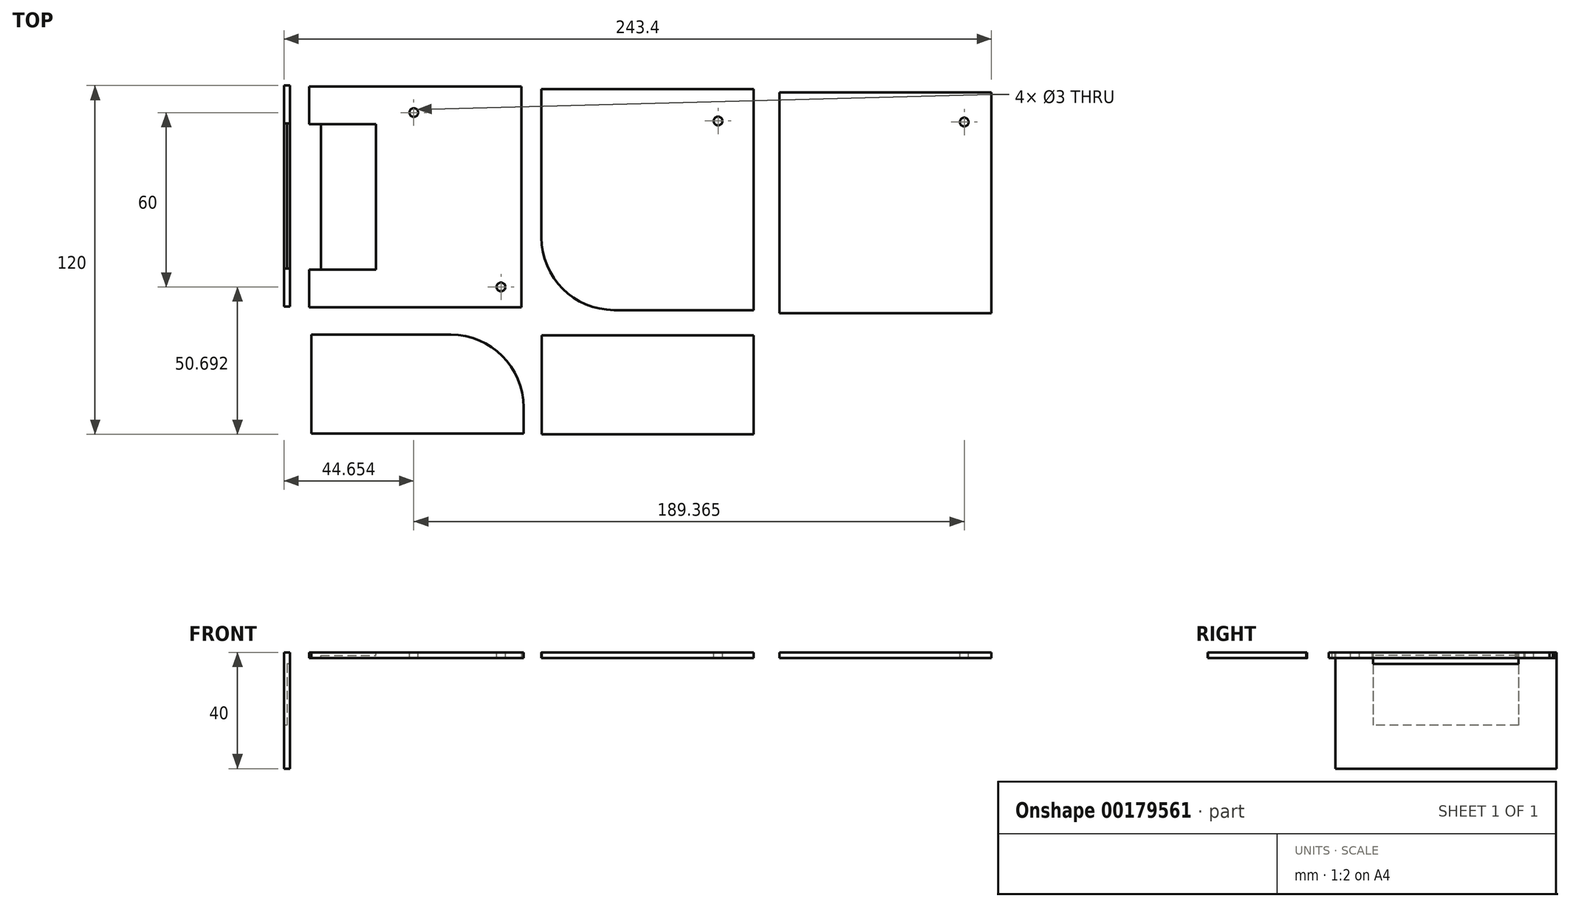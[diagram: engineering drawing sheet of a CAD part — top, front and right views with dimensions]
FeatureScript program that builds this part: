
annotation { "Feature Type Name" : "Feature", "Feature Type Description" : "" }
export const myFeature = defineFeature(function(context is Context, id is Id, definition is map)
    precondition{}
    {
        {
            var Q0;
            Q0=qCreatedBy(makeId("Top.planeOp"),FACE);
            var sketch = newSketch(context, id + "F0", { "sketchPlane" : qUnion([Q0])});
            skLineSegment(sketch, "E0.bottom", {"start": v(-79.9, 85.7) * mm, "end": v(-6.9, 85.7) * mm});
            skLineSegment(sketch, "E0.top", {"start": v(-79.9, 9.7) * mm, "end": v(-6.9, 9.7) * mm});
            skLineSegment(sketch, "E0.left", {"start": v(-79.9, 85.7) * mm, "end": v(-79.9, 9.7) * mm});
            skLineSegment(sketch, "E0.right", {"start": v(-6.9, 85.7) * mm, "end": v(-6.9, 9.7) * mm});
            skSolve(sketch);
        }
        {
            var Q0;
            Q0=qSketchRegion(id+"F0",true);
            extrude(context, id + "F1", {"entities" : qUnion([Q0]), "depth" : 2 * mm});
        }
        {
            var Q0;
            Q0=qCreatedBy(makeId("Top.planeOp"),FACE);
            var sketch = newSketch(context, id + "F2", { "sketchPlane" : qUnion([Q0])});
            skLineSegment(sketch, "E1.bottom", {"start": v(0, 84.75) * mm, "end": v(73, 84.75) * mm});
            skLineSegment(sketch, "E1.top", {"start": v(25, 8.75) * mm, "end": v(73, 8.75) * mm});
            skLineSegment(sketch, "E1.left", {"start": v(0, 84.75) * mm, "end": v(0, 33.75) * mm});
            skLineSegment(sketch, "E1.right", {"start": v(73, 84.75) * mm, "end": v(73, 8.75) * mm});
            skPoint(sketch, "E2.visualSharp", {"position": v(0, 8.75) * mm});
            skArc(sketch, "E2.filletArc", {"start": v(0, 33.75) * mm, "mid": v(7.33, 16.07) * mm, "end": v(25, 8.75) * mm});
            skSolve(sketch);
        }
        {
            var Q0;
            Q0=qSketchRegion(id+"F2",true);
            extrude(context, id + "F3", {"entities" : qUnion([Q0]), "depth" : 2 * mm});
        }
        {
            var Q0;
            Q0=qCreatedBy(makeId("Top.planeOp"),FACE);
            var sketch = newSketch(context, id + "F4", { "sketchPlane" : qUnion([Q0])});
            skLineSegment(sketch, "E3.bottom", {"start": v(-79.15, 0.26) * mm, "end": v(-31.15, 0.26) * mm});
            skLineSegment(sketch, "E3.top", {"start": v(-79.15, -33.74) * mm, "end": v(-6.15, -33.74) * mm});
            skLineSegment(sketch, "E3.left", {"start": v(-79.15, 0.26) * mm, "end": v(-79.15, -33.74) * mm});
            skLineSegment(sketch, "E3.right", {"start": v(-6.15, -24.74) * mm, "end": v(-6.15, -33.74) * mm});
            skPoint(sketch, "E4.visualSharp", {"position": v(-6.15, 0.26) * mm});
            skArc(sketch, "E4.filletArc", {"start": v(-6.15, -24.74) * mm, "mid": v(-13.47, -7.06) * mm, "end": v(-31.15, 0.26) * mm});
            skSolve(sketch);
        }
        {
            var Q0;
            Q0=qSketchRegion(id+"F4",true);
            extrude(context, id + "F5", {"entities" : qUnion([Q0]), "depth" : 2 * mm});
        }
        {
            var Q0;
            Q0=qCreatedBy(makeId("Top.planeOp"),FACE);
            var sketch = newSketch(context, id + "F6", { "sketchPlane" : qUnion([Q0])});
            skLineSegment(sketch, "E5.bottom", {"start": v(0.04, 0) * mm, "end": v(73.04, 0) * mm});
            skLineSegment(sketch, "E5.top", {"start": v(0.04, -34) * mm, "end": v(73.04, -34) * mm});
            skLineSegment(sketch, "E5.left", {"start": v(0.04, 0) * mm, "end": v(0.04, -34) * mm});
            skLineSegment(sketch, "E5.right", {"start": v(73.04, 0) * mm, "end": v(73.04, -34) * mm});
            skSolve(sketch);
        }
        {
            var Q0;
            Q0=qSketchRegion(id+"F6",true);
            extrude(context, id + "F7", {"entities" : qUnion([Q0]), "depth" : 2 * mm});
        }
        {
            var Q0;
            Q0=qCreatedBy(makeId("Top.planeOp"),FACE);
            var sketch = newSketch(context, id + "F8", { "sketchPlane" : qUnion([Q0])});
            skLineSegment(sketch, "E6.bottom", {"start": v(81.84, 83.66) * mm, "end": v(154.84, 83.66) * mm});
            skLineSegment(sketch, "E6.top", {"start": v(81.84, 7.66) * mm, "end": v(154.84, 7.66) * mm});
            skLineSegment(sketch, "E6.left", {"start": v(81.84, 83.66) * mm, "end": v(81.84, 7.66) * mm});
            skLineSegment(sketch, "E6.right", {"start": v(154.84, 83.66) * mm, "end": v(154.84, 7.66) * mm});
            skSolve(sketch);
        }
        {
            var Q0;
            Q0=makeQuery(id+"F8.imprint","IMPRINT",FACE,{"disambiguationData":[TD([[makeQuery(id+"F8.imprint","IMPRINT",EDGE,{"derivedFrom":sQuery(id+"F8.wireOp",EDGE,"E6.bottom")}),-1.0]])]});
            extrude(context, id + "F9", {"entities" : qUnion([Q0]), "depth" : 2 * mm});
        }
        {
            var Q0;
            Q0=qCreatedBy(makeId("Top.planeOp"),FACE);
            var sketch = newSketch(context, id + "F10", { "sketchPlane" : qUnion([Q0])});
            skLineSegment(sketch, "E7.bottom", {"start": v(121.44, 0) * mm, "end": v(121.44, -76) * mm});
            skLineSegment(sketch, "E7.top", {"start": v(81.44, 0) * mm, "end": v(81.44, -76) * mm});
            skLineSegment(sketch, "E7.left", {"start": v(121.44, 0) * mm, "end": v(81.44, 0) * mm});
            skLineSegment(sketch, "E7.right", {"start": v(121.44, -76) * mm, "end": v(81.44, -76) * mm});
            skLineSegment(sketch, "E8.bottom", {"start": v(168.25, 0) * mm, "end": v(168.25, -76) * mm});
            skLineSegment(sketch, "E8.top", {"start": v(128.25, 0) * mm, "end": v(128.25, -76) * mm});
            skLineSegment(sketch, "E8.left", {"start": v(168.25, 0) * mm, "end": v(128.25, 0) * mm});
            skLineSegment(sketch, "E8.right", {"start": v(168.25, -76) * mm, "end": v(128.25, -76) * mm});
            skSolve(sketch);
        }
        {
            var Q0;
            Q0=qSketchRegion(id+"F10",true);
            extrude(context, id + "F11", {"entities" : qUnion([Q0]), "depth" : 2 * mm});
        }
        {
            var Q0;
            Q0=makeQuery(id+"F11.opExtrude","SWEPT_BODY",BODY,{"disambiguationData":[OSD([sQuery(id+"F10.wireOp",EDGE,"E8.bottom"),sQuery(id+"F10.wireOp",EDGE,"E8.top"),sQuery(id+"F10.wireOp",EDGE,"E8.left"),sQuery(id+"F10.wireOp",EDGE,"E8.right")])]});
            deleteBodies(context, id + "F12", {"entities" : qUnion([Q0])});
        }
        {
            var Q0;
            Q0=makeQuery(id+"F1.opExtrude","CAP_FACE",FACE,{"disambiguationData":[OSD([sQuery(id+"F0.wireOp",EDGE,"E0.bottom"),sQuery(id+"F0.wireOp",EDGE,"E0.top"),sQuery(id+"F0.wireOp",EDGE,"E0.left"),sQuery(id+"F0.wireOp",EDGE,"E0.right")])],"isStart":false});
            var sketch = newSketch(context, id + "F13", { "sketchPlane" : qUnion([Q0])});
            skCircle(sketch, "E9", {"center": v(-13.9, 16.7) * mm, "radius": 1.5 * mm});
            skCircle(sketch, "E10", {"center": v(-43.9, 76.7) * mm, "radius": 1.5 * mm});
            skCircle(sketch, "E11", {"center": v(60.77, 73.78) * mm, "radius": 1.5 * mm});
            skCircle(sketch, "E12", {"center": v(145.46, 73.43) * mm, "radius": 1.5 * mm});
            skLineSegment(sketch, "E13", {"start": v(-43.9, 76.7) * mm, "end": v(-43.9, 85.7) * mm, "construction": true});
            skLineSegment(sketch, "E14", {"start": v(-43.9, 76.7) * mm, "end": v(-6.9, 76.7) * mm, "construction": true});
            skLineSegment(sketch, "E15", {"start": v(-13.9, 16.7) * mm, "end": v(-13.9, 9.7) * mm, "construction": true});
            skLineSegment(sketch, "E16", {"start": v(-13.9, 16.7) * mm, "end": v(-6.9, 16.7) * mm, "construction": true});
            skLineSegment(sketch, "E17", {"start": v(60.77, 73.78) * mm, "end": v(72.77, 73.78) * mm, "construction": true});
            skLineSegment(sketch, "E18", {"start": v(145.46, 73.43) * mm, "end": v(154.46, 73.43) * mm, "construction": true});
            skLineSegment(sketch, "E19", {"start": v(145.46, 73.43) * mm, "end": v(145.46, 83.43) * mm, "construction": true});
            skSolve(sketch);
        }
        {
            var Q0;
            Q0=makeQuery(id+"F13.imprint","IMPRINT",FACE,{"disambiguationData":[TD([[makeQuery(id+"F13.imprint","IMPRINT",EDGE,{"derivedFrom":sQuery(id+"F13.wireOp",EDGE,"E11")}),1.0]])]});
            var Q1;
            Q1=makeQuery(id+"F13.imprint","IMPRINT",FACE,{"disambiguationData":[TD([[makeQuery(id+"F13.imprint","IMPRINT",EDGE,{"derivedFrom":sQuery(id+"F13.wireOp",EDGE,"E12")}),1.0]])]});
            var Q2;
            Q2=makeQuery(id+"F13.imprint","IMPRINT",FACE,{"disambiguationData":[TD([[makeQuery(id+"F13.imprint","IMPRINT",EDGE,{"derivedFrom":sQuery(id+"F13.wireOp",EDGE,"E9")}),1.0]])]});
            var Q3;
            Q3=makeQuery(id+"F13.imprint","IMPRINT",FACE,{"disambiguationData":[TD([[makeQuery(id+"F13.imprint","IMPRINT",EDGE,{"derivedFrom":sQuery(id+"F13.wireOp",EDGE,"E10")}),1.0]])]});
            var Q4;
            Q4=qConstructionFilter(qBodyType(qCreatedBy(id+"F13",EDGE),BodyType.WIRE),ConstructionObject.NO);
            extrude(context, id + "F14", {"entities" : qUnion([Q0, Q1, Q2, Q3]), "operationType" : NewBodyOperationType.REMOVE, "surfaceEntities" : qUnion([Q4]), "oppositeDirection" : true, "depth" : 3 * mm});
        }
        {
            var Q0;
            Q0=makeQuery(id+"F11.opExtrude","SWEPT_BODY",BODY,{"disambiguationData":[OSD([sQuery(id+"F10.wireOp",EDGE,"E7.bottom"),sQuery(id+"F10.wireOp",EDGE,"E7.top"),sQuery(id+"F10.wireOp",EDGE,"E7.left"),sQuery(id+"F10.wireOp",EDGE,"E7.right")])]});
            transform(context, id + "F15", {"entities" : qUnion([Q0]), "transformType" : TransformType.TRANSLATION_3D, "dx" : -210 * mm, "dy" : 86 * mm, "dz" : 0 * mm, "makeCopy" : false});
        }
        {
            var Q0;
            Q0=makeQuery(id+"F11.opExtrude","SWEPT_BODY",BODY,{"disambiguationData":[OSD([sQuery(id+"F10.wireOp",EDGE,"E7.bottom"),sQuery(id+"F10.wireOp",EDGE,"E7.top"),sQuery(id+"F10.wireOp",EDGE,"E7.left"),sQuery(id+"F10.wireOp",EDGE,"E7.right")])]});
            var Q1;
            Q1=makeQuery(id+"F11.opExtrude","CAP_EDGE",EDGE,{"disambiguationData":[OSD([sQuery(id+"F10.wireOp",EDGE,"E7.bottom")])],"isStart":false});
            transform(context, id + "F16", {"entities" : qUnion([Q0]), "transformType" : TransformType.ROTATION, "transformAxis" : qUnion([Q1]), "angle" : 90 * degree, "makeCopy" : false});
        }
        {
            var Q0;
            Q0=makeQuery(id+"F1.opExtrude","CAP_FACE",FACE,{"disambiguationData":[OSD([sQuery(id+"F0.wireOp",EDGE,"E0.bottom"),sQuery(id+"F0.wireOp",EDGE,"E0.top"),sQuery(id+"F0.wireOp",EDGE,"E0.left"),sQuery(id+"F0.wireOp",EDGE,"E0.right")])],"isStart":false});
            var sketch = newSketch(context, id + "F17", { "sketchPlane" : qUnion([Q0])});
            skLineSegment(sketch, "E20.bottom", {"start": v(-79.9, 72.7) * mm, "end": v(-56.9, 72.7) * mm});
            skLineSegment(sketch, "E20.top", {"start": v(-79.9, 22.7) * mm, "end": v(-56.9, 22.7) * mm});
            skLineSegment(sketch, "E20.left", {"start": v(-79.9, 72.7) * mm, "end": v(-79.9, 22.7) * mm});
            skLineSegment(sketch, "E20.right", {"start": v(-56.9, 72.7) * mm, "end": v(-56.9, 22.7) * mm});
            skLineSegment(sketch, "E21", {"start": v(-56.9, 72.7) * mm, "end": v(-56.9, 85.7) * mm, "construction": true});
            skSolve(sketch);
        }
        {
            var Q0;
            Q0=qSketchRegion(id+"F17",true);
            extrude(context, id + "F18", {"entities" : qUnion([Q0]), "operationType" : NewBodyOperationType.REMOVE, "oppositeDirection" : true, "depth" : 1 * mm});
        }
        {
            var Q0;
            Q0=makeQuery(id+"F18.boolean.opBoolean","COPY",FACE,{"derivedFrom":makeQuery(id+"F18.opExtrude","CAP_FACE",FACE,{"disambiguationData":[OSD([sQuery(id+"F17.wireOp",EDGE,"E20.bottom"),sQuery(id+"F17.wireOp",EDGE,"E20.top"),sQuery(id+"F17.wireOp",EDGE,"E20.left"),sQuery(id+"F17.wireOp",EDGE,"E20.right")])],"isStart":false})});
            var sketch = newSketch(context, id + "F19", { "sketchPlane" : qUnion([Q0])});
            skLineSegment(sketch, "E22.bottom", {"start": v(-79.9, 72.7) * mm, "end": v(-75.9, 72.7) * mm});
            skLineSegment(sketch, "E22.top", {"start": v(-79.9, 22.7) * mm, "end": v(-75.9, 22.7) * mm});
            skLineSegment(sketch, "E22.left", {"start": v(-79.9, 72.7) * mm, "end": v(-79.9, 22.7) * mm});
            skLineSegment(sketch, "E22.right", {"start": v(-75.9, 72.7) * mm, "end": v(-75.9, 22.7) * mm});
            skSolve(sketch);
        }
        {
            var Q0;
            Q0=qSketchRegion(id+"F19",true);
            extrude(context, id + "F20", {"entities" : qUnion([Q0]), "operationType" : NewBodyOperationType.REMOVE, "oppositeDirection" : true, "depth" : 2 * mm});
        }
        {
            var Q0;
            Q0=makeQuery(id+"F11.opExtrude","CAP_FACE",FACE,{"disambiguationData":[OSD([sQuery(id+"F10.wireOp",EDGE,"E7.bottom"),sQuery(id+"F10.wireOp",EDGE,"E7.top"),sQuery(id+"F10.wireOp",EDGE,"E7.left"),sQuery(id+"F10.wireOp",EDGE,"E7.right")])],"isStart":false});
            var sketch = newSketch(context, id + "F21", { "sketchPlane" : qUnion([Q0])});
            skLineSegment(sketch, "E23.bottom", {"start": v(-73, 2) * mm, "end": v(-23, 2) * mm});
            skLineSegment(sketch, "E23.top", {"start": v(-73, -23) * mm, "end": v(-23, -23) * mm});
            skLineSegment(sketch, "E23.left", {"start": v(-73, 2) * mm, "end": v(-73, -23) * mm});
            skLineSegment(sketch, "E23.right", {"start": v(-23, 2) * mm, "end": v(-23, -23) * mm});
            skLineSegment(sketch, "E24", {"start": v(-23, -23) * mm, "end": v(-10, -23) * mm, "construction": true});
            skSolve(sketch);
        }
        {
            var Q0;
            Q0=qSketchRegion(id+"F21",true);
            extrude(context, id + "F22", {"entities" : qUnion([Q0]), "operationType" : NewBodyOperationType.REMOVE, "oppositeDirection" : true, "depth" : 1 * mm});
        }
        {
            var Q0;
            Q0=makeQuery(id+"F22.boolean.opBoolean","COPY",FACE,{"derivedFrom":makeQuery(id+"F22.opExtrude","CAP_FACE",FACE,{"disambiguationData":[OSD([sQuery(id+"F21.wireOp",EDGE,"E23.bottom"),sQuery(id+"F21.wireOp",EDGE,"E23.top"),sQuery(id+"F21.wireOp",EDGE,"E23.left"),sQuery(id+"F21.wireOp",EDGE,"E23.right")])],"isStart":false})});
            var sketch = newSketch(context, id + "F23", { "sketchPlane" : qUnion([Q0])});
            skLineSegment(sketch, "E25.bottom", {"start": v(-73, 2) * mm, "end": v(-23, 2) * mm});
            skLineSegment(sketch, "E25.top", {"start": v(-73, -2) * mm, "end": v(-23, -2) * mm});
            skLineSegment(sketch, "E25.left", {"start": v(-73, 2) * mm, "end": v(-73, -2) * mm});
            skLineSegment(sketch, "E25.right", {"start": v(-23, 2) * mm, "end": v(-23, -2) * mm});
            skSolve(sketch);
        }
        {
            var Q0;
            Q0=qSketchRegion(id+"F23",true);
            extrude(context, id + "F24", {"entities" : qUnion([Q0]), "operationType" : NewBodyOperationType.REMOVE, "oppositeDirection" : true, "depth" : 1.5 * mm});
        }
    });
